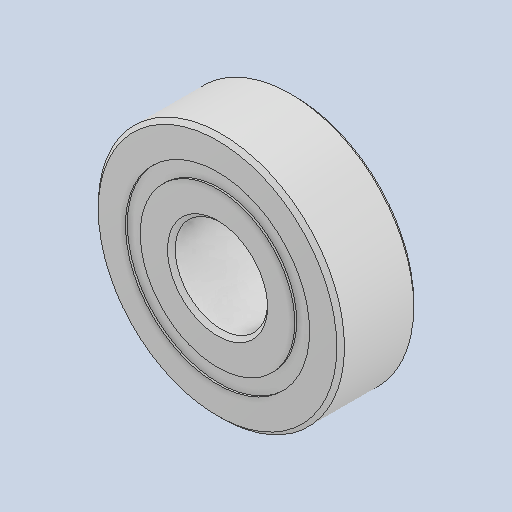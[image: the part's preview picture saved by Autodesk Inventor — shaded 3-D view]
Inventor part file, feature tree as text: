
AUTODESK INVENTOR PART (.ipt)
format: ipt  version: 2022 (Build 260153000, 153)  size: 569,344 bytes
history: mixed  units: mm
features: other x11, revolve x5, imported_body x1
ambient origin geometry x8: Origin, YZ Plane, XZ Plane, XY Plane, X Axis, Y Axis, Z Axis, Center Point
bodies: Solid1 (imported_parasolid), Solid2 (imported_parasolid), Solid3 (imported_parasolid), Solid4 (imported_parasolid), Solid5 (imported_parasolid), Solid6 (imported_parasolid), Solid7 (imported_parasolid), Solid8 (imported_parasolid), Solid9 (imported_parasolid), Solid10 (imported_parasolid), Solid11 (imported_parasolid), Solid12 (imported_parasolid), Solid13 (imported_parasolid), Solid14 (imported_parasolid), Solid15 (imported_parasolid), Solid16 (imported_parasolid)
feature tree (17):
  revolve  "Revolve1"  [1 undecoded]
  revolve  "Revolve3"  [1 undecoded]
  revolve  "Revolve4"  [1 undecoded]
  other  "CirPattern1[1]"
  other  "CirPattern1[2]"
  other  "CirPattern1[3]"
  other  "CirPattern1[4]"
  other  "CirPattern1[5]"
  other  "CirPattern1[6]"
  other  "CirPattern1[7]"
  other  "CirPattern1[8]"
  other  "CirPattern1[9]"
  other  "CirPattern1[10]"
  other  "CirPattern1[11]"
  revolve  "Revolve5[1]"  [1 undecoded]
  revolve  "Revolve5[2]"  [1 undecoded]
  imported_body  NMx_Import_Brep_tag  [imported B-rep: ~36 faces, bbox_mm=[10.0, 0.0, 10.0]]
note: 5 required parameter values undecoded (feature->parameter linkage not recoverable at this tier; creation-order binding heuristic only, values carry confidence <= 0.55)
